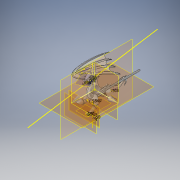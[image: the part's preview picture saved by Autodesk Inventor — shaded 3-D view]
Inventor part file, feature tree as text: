
AUTODESK INVENTOR PART (.ipt)
format: ipt  version: 2018 (Build 220112000, 112)  size: 5,354,496 bytes
history: native  units: in
note: dims shown in document units (in); Inventor stores cm internally (conversion verified against a paired STEP export)
features: sketch x122, plane x56, loft x36, fillet x16, other x14, projected_geometry x11, extrude x9, mirror x8, revolve x3, chamfer x2
ambient origin geometry x8: Origin, YZ Plane, XZ Plane, XY Plane, X Axis, Y Axis, Z Axis, Center Point
bodies: Solid1 (feature_tree)
feature tree (277):
  sketch  "Sketch4"  dims[d4=0.4in d5=0.4in]
  sketch  "Sketch5"  dims[d6=0.0in d7=0.0in]
  plane  "Work Plane2"
  loft  "Loft1"
  plane  "Work Plane4"
  sketch  "Sketch8"  dims[d10=0.0in d11=0.0in]
  plane  "Work Plane5"
  loft  "Loft2"
  extrude  "Extrusion1"  Depth=0.55in
  plane  "Work Plane6"
  extrude  "Extrusion2"  TaperAngle=0.0deg  [1 undecoded]
  extrude  "Extrusion3"  TaperAngle=0.0deg  [1 undecoded]
  chamfer  "Chamfer1"  Angle=90.0deg  [1 undecoded]
  sketch  "Sketch22"  dims[d39=0.45in d40=0.35in]
  plane  "Work Plane13"
  sketch  "Sketch23"  dims[d41=0.35in d42=0.5in]
  plane  "Work Plane14"
  loft  "Loft4"
  sketch  "Sketch25"  dims[d46=0.55in d47=0.0in]
  sketch  "Sketch26"  dims[d48=0.0in d49=0.35in d50=0.5in d51=0.0in d52=0.0in d53=90.0deg d54=0.0in d55=90.0deg d56=0.0in d57=90.0deg d58=1.0in]
  plane  "Work Plane15"
  sketch  "Sketch27"  dims[d59=1.0in d60=0.0in d61=0.25in]
  plane  "Work Plane16"
  loft  "Loft5"
  fillet  "Fillet1"  [1 undecoded]
  plane  "Work Plane17"
  sketch  "Sketch29"  dims[d64=1.2in d65=0.125in d66=0.15in d67=1.0in d68=0.0in d69=0.125in d70=0.0in]
  plane  "Work Plane18"
  loft  "Loft7"
  sketch  "Sketch32"  dims[d107=0.55in d108=-0.8in]
  plane  "Work Plane21"
  sketch  "Sketch35"  dims[d109=0.5in d110=0.5in]
  plane  "Work Plane22"
  loft  "Loft8"
  plane  "Work Plane23"
  sketch  "Sketch37"  dims[d112=0.89in d113=0.0in d114=90.0deg d115=0.0in d116=90.0deg]
  sketch  "Sketch38"  dims[d117=0.0in d118=90.0deg d119=0.65in d120=0.4in]
  sketch  "Sketch39"  dims[d121=0.5in d123=0.6in]
  plane  "Work Plane25"
  loft  "Loft9"
  sketch  "Sketch43"  dims[d132=0.15in d133=0.75in]
  sketch  "Sketch44"  dims[d134=0.3in d135=0.2in]
  sketch  "Sketch45"  dims[d136=0.5in d141=0.0in d142=90.0deg]
  plane  "Work Plane27"
  loft  "Loft11"
  fillet  "Fillet2"  [1 undecoded]
  other  "Work Point3"
  sketch  "Sketch48"  dims[d155=0.124in d156=90.0deg d157=-0.75in]
  sketch  "Sketch49"  dims[d158=1.0in d159=0.55in]
  plane  "Work Plane28"
  extrude  "Extrusion4"  TaperAngle=0.0deg  [1 undecoded]
  mirror  "Mirror3"
  extrude  "Extrusion6"  Depth=0.35in
  fillet  "Fillet3"  Radius=0.5in
  fillet  "Fillet4"  [1 undecoded]
  fillet  "Fillet12"  [1 undecoded]
  fillet  "Fillet9"  [1 undecoded]
  fillet  "Fillet10"  [1 undecoded]
  fillet  "Fillet11"  Radius=1.0in
  mirror  "Mirror4"
  mirror  "Mirror5"
  mirror  "Mirror6"
  plane  "Work Plane29"
  sketch  "Sketch52"  dims[d167=0.35in d168=0.7in]
  plane  "Work Plane30"
  sketch  "Sketch54"  dims[d169=0.65in d170=0.6in]
  sketch  "Sketch55"  dims[d171=0.2in d172=0.0in d173=90.0deg]
  plane  "Work Plane31"
  sketch  "Sketch56"  dims[d174=0.0in d175=90.0deg d176=0.0in d177=90.0deg d179=0.5in]
  sketch  "Sketch57"  dims[d180=-0.1in d181=0.2in]
  plane  "Work Plane34"
  sketch  "Sketch60"  dims[d182=0.28in d187=0.7in]
  loft  "Loft14"
  loft  "Loft15"
  sketch  "Sketch61"  dims[d188=0.7in d189=0.0in d190=90.0deg]
  sketch  "Sketch62"  dims[d191=0.0in d192=90.0deg d193=0.0in d194=90.0deg d196=0.125in]
  plane  "Work Plane35"
  loft  "Loft16"
  fillet  "Fillet14"  Radius=0.15in
  fillet  "Fillet15"  Radius=1.0in
  mirror  "Mirror7"
  fillet  "Fillet16"  Radius=0.125in
  sketch  "Sketch64"  dims[d200=1.25in d201=1.55in]
  sketch  "Sketch65"  dims[d202=0.175in d203=0.25in]
  plane  "Work Plane36"
  loft  "Loft17"
  loft  "Loft18"
  sketch  "Sketch70"  dims[d221=-0.45in]
  plane  "Work Plane37"
  sketch  "Sketch71"  dims[d222=0.4in]
  plane  "Work Plane38"
  revolve  "Revolution1"  [1 undecoded]
  extrude  "Extrusion7"  Depth=0.5in
  chamfer  "Chamfer2"  Angle=90.0deg  [1 undecoded]
  mirror  "Mirror8"
  fillet  "Fillet19"  [1 undecoded]
  plane  "Work Plane39"
  sketch  "Sketch74"  dims[d225=0.0in]
  sketch  "Sketch75"  dims[d226=0.45in]
  plane  "Work Plane40"
  revolve  "Revolution2"  [1 undecoded]
  fillet  "Fillet21"  Radius=0.4in
  sketch  "Sketch77"  dims[d228=0.0in]
  sketch  "Sketch78"  dims[d229=0.0in]
  plane  "Work Plane41"
  sketch  "Sketch79"  dims[d232=-0.4in]
  plane  "Work Plane42"
  loft  "Loft19"
  plane  "Work Plane43"
  extrude  "Extrusion8"  Depth=0.2in
  plane  "Work Plane44"
  sketch  "Sketch82"  dims[d235=0.0in]
  plane  "Work Plane45"
  sketch  "Sketch83"  dims[d236=0.0in]
  fillet  "Fillet22"  [1 undecoded]
  loft  "Loft21"
  sketch  "Sketch85"  dims[d238=0.525in]
  sketch  "Sketch86"  dims[d239=0.35in]
  sketch  "Sketch87"  dims[d240=0.45in]
  sketch  "Sketch88"  dims[d241=0.4in]
  plane  "Work Plane46"
  sketch  "Sketch89"  dims[d256=0.3in]
  plane  "Work Plane47"
  sketch  "Sketch90"  dims[d257=0.0in d258=90.0deg]
  plane  "Work Plane48"
  sketch  "Sketch91"  dims[d259=0.0in d260=90.0deg]
  other  "Work Point4"
  loft  "Loft22"
  plane  "Work Plane49"
  sketch  "Sketch92"  dims[d261=0.0in d262=90.0deg]
  other  "Work Point5"
  loft  "Loft23"
  plane  "Work Plane50"
  sketch  "Sketch93"  dims[d263=0.0in d264=90.0deg]
  other  "Work Point6"
  loft  "Loft24"
  plane  "Work Plane51"
  sketch  "Sketch94"  dims[d265=0.0in d266=90.0deg]
  sketch  "Sketch95"  dims[d267=0.0in d268=90.0deg]
  other  "Work Point7"
  loft  "Loft25"
  plane  "Work Plane52"
  sketch  "Sketch96"  dims[d270=0.45in d271=0.55in d272=0.89in]
  sketch  "Sketch97"  dims[d276=0.4in]
  other  "Work Point8"
  loft  "Loft26"
  mirror  "Mirror9"
  sketch  "Sketch98"  dims[d277=0.065in]
  sketch  "Sketch99"  dims[d278=0.5in]
  sketch  "Sketch100"  dims[d279=0.55in]
  plane  "Work Plane53"
  sketch  "Sketch101"  dims[d280=0.5622in]
  sketch  "Sketch102"  dims[d281=0.5544in]
  other  "Work Point9"
  loft  "Loft27"
  plane  "Work Plane54"
  loft  "Loft28"
  sketch  "Sketch105"  dims[d287=0.0in d288=90.0deg]
  plane  "Work Plane55"
  loft  "Loft29"
  sketch  "Sketch107"  dims[d291=0.05in]
  plane  "Work Plane56"
  loft  "Loft30"
  sketch  "Sketch109"  dims[d293=0.1388in]
  plane  "Work Plane57"
  loft  "Loft31"
  sketch  "Sketch111"  dims[d295=0.4in]
  plane  "Work Plane58"
  loft  "Loft32"
  sketch  "Sketch113"  dims[d297=0.6in]
  sketch  "Sketch114"  dims[d298=0.2in]
  plane  "Work Plane59"
  revolve  "Revolution3"  Angle=90.0deg
  extrude  "Extrusion9"  TaperAngle=0.0deg  [1 undecoded]
  mirror  "Mirror10"
  fillet  "Fillet23"  Radius=0.5in
  plane  "Work Plane60"
  sketch  "Sketch119"  dims[d303=0.0in d304=90.0deg]
  plane  "Work Plane61"
  sketch  "Sketch120"  dims[d305=0.5in]
  plane  "Work Plane62"
  loft  "Loft33"
  loft  "Loft34"
  plane  "Work Plane65"
  sketch  "Sketch122"  dims[d307=0.75in]
  plane  "Work Plane66"
  sketch  "Sketch123"  dims[d308=0.2in]
  plane  "Work Plane68"
  sketch  "Sketch124"  dims[d309=0.3in]
  other  "Work Point10"
  loft  "Loft35"
  sketch  "Sketch126"  dims[d312=0.0in d313=90.0deg]
  sketch  "Sketch127"  dims[d314=0.1in]
  other  "Work Point11"
  loft  "Loft36"
  fillet  "Fillet24"  Radius=0.125in
  sketch  "Sketch128"  dims[d315=0.4in]
  sketch  "Sketch129"  dims[d316=0.75in]
  other  "Work Point12"
  loft  "Loft37"
  extrude  "Extrusion10"  Depth=1.55in
  plane  "Work Plane69"
  loft  "Loft38"
  sketch  "Sketch132"  dims[d319=1.3in]
  plane  "Work Plane71"
  sketch  "Sketch133"  dims[d320=0.45in]
  sketch  "Sketch134"  dims[d321=0.6in]
  loft  "Loft39"
  loft  "Loft40"
  loft  "Loft41"
  loft  "Loft42"
  sketch  "Sketch6"  dims[d8=0.55in d9=0.55in]
  sketch  "Sketch9"  dims[d12=0.5in d13=0.0in d14=90.0deg d15=0.0in d16=90.0deg]
  other  "Edges1"
  sketch  "Sketch10"  dims[d17=0.0in d18=90.0deg d19=3.0in]
  projected_geometry  "Projected Loop2"
  projected_geometry  "Projected Loop3"
  sketch  "Sketch11"  dims[d21=0.65in d34=0.0in d35=0.0in]
  projected_geometry  "Projected Loop4"
  sketch  "Sketch12"  dims[d36=0.0in d38=0.0in]
  projected_geometry  "Projected Loop5"
  sketch  "Sketch24"  dims[d43=-0.7in d44=0.35in d45=0.0in]
  sketch  "Sketch28"  dims[d62=2.0in d63=0.6in]
  sketch  "Sketch30"  dims[d75=0.03in d76=0.125in d77=45.0deg d103=0.1in]
  sketch  "Sketch31"  dims[d104=0.5in d106=0.45in]
  plane  "Work Plane20"
  sketch  "Sketch36"  dims[d111=0.55in]
  projected_geometry  "Projected Loop8"
  sketch  "Sketch40"  dims[d124=0.0in d125=0.2in d126=0.0in d127=90.0deg]
  sketch  "Sketch41"  dims[d128=0.0in d129=90.0deg d130=0.0in d131=90.0deg]
  plane  "Work Plane26"
  sketch  "Sketch46"  dims[d143=0.0in d144=90.0deg d146=0.5in d147=0.45in d148=0.55in d149=0.89in]
  sketch  "Sketch47"  dims[d150=45.0deg d154=0.535in]
  sketch  "Sketch50"  dims[d160=0.0in d161=90.0deg d162=0.0in d163=90.0deg]
  sketch  "Sketch51"  dims[d164=0.0in d165=90.0deg d166=-0.5in]
  projected_geometry  "Projected Loop9"
  other  "Edges4"
  other  "Edges5"
  sketch  "Sketch63"  dims[d198=0.5in d199=1.2in]
  projected_geometry  "Projected Loop10"
  sketch  "Sketch66"  dims[d204=0.25in d205=0.0in d208=0.125in d209=0.0in]
  sketch  "Sketch67"  dims[d210=0.075in d211=0.05in]
  sketch  "Sketch68"  dims[d216=0.075in d217=0.05in]
  sketch  "Sketch69"  dims[d218=0.065in d219=0.065in]
  projected_geometry  "Projected Loop11"
  sketch  "Sketch72"  dims[d223=0.4in]
  sketch  "Sketch73"  dims[d224=0.0in]
  projected_geometry  "Projected Loop12"
  sketch  "Sketch76"  dims[d227=0.6in]
  sketch  "Sketch80"  dims[d233=0.0in]
  sketch  "Sketch81"  dims[d234=0.0in]
  projected_geometry  "Projected Loop13"
  sketch  "Sketch84"  dims[d237=0.35in]
  projected_geometry  "Projected Loop14"
  sketch  "Sketch103"  dims[d284=0.52in]
  sketch  "Sketch104"  dims[d285=0.0in d286=90.0deg]
  sketch  "Sketch106"  dims[d289=0.0in d290=90.0deg]
  sketch  "Sketch108"  dims[d292=0.125in]
  sketch  "Sketch110"  dims[d294=0.65in]
  sketch  "Sketch112"  dims[d296=0.5in]
  sketch  "Sketch115"  dims[d299=0.0in d300=90.0deg]
  sketch  "Sketch116"  dims[d301=0.0in d302=90.0deg]
  sketch  "Sketch121"  dims[d306=0.8176in]
  other  "Edges6"
  sketch  "Sketch125"  dims[d310=0.0in d311=90.0deg]
  sketch  "Sketch130"  dims[d317=90.0deg]
  sketch  "Sketch131"  dims[d318=0.75in]
  plane  "Work Plane70"
  sketch  "Sketch136"  dims[d322=0.2in d323=0.0in]
  sketch  "Sketch137"  dims[d324=0.1in d325=0.125in d326=45.0deg]
  sketch  "Sketch138"  dims[d327=0.5944in]
  sketch  "Sketch139"  dims[d330=10.0in]
  sketch  "Sketch140"  dims[d331=10.0in]
  sketch  "Sketch141"  dims[d332=2.0in]
  sketch  "Sketch142"  dims[d333=0.6252in]
  sketch  "Sketch143"  dims[d334=0.475in]
  sketch  "Sketch144"  dims[d335=0.045in d336=-1.0in d337=2.5in d338=0.3in d339=0.6in d340=1.25in d341=1.25in d344=30.0deg d346=0.125in d347=1.0in d348=0.5in d349=0.5in d350=0.5in d351=0.225in d352=0.25in d353=-0.4in d354=0.2in d355=0.06in d356=0.0in d357=90.0deg d358=0.0in d359=90.0deg d360=0.5in d361=0.5in d362=0.3125in d363=0.0in d364=0.15in d365=0.02in d366=0.175in d367=-0.6in d368=0.12in d376=0.03in d377=0.25in d378=0.0in d379=90.0deg d380=0.3937in d381=90.0deg d382=0.0in d383=90.0deg d384=0.2in d385=0.45in d388=0.2in d389=0.18in d391=0.175in d392=0.555in d393=0.27in d394=0.28in d395=0.645in d396=0.655in d397=0.678in d398=0.2in d399=0.2in d401=0.3in d402=0.35in d403=0.6in d404=0.55in d405=0.325in d406=0.6in d407=0.25in d408=0.5in d409=0.2in d410=0.45in d411=0.2in d412=0.18in d413=0.175in d414=0.555in d415=0.27in d416=0.28in d417=0.645in d418=0.655in d419=0.678in d424=-0.5in d425=0.2in d426=0.45in d427=0.2in d428=0.18in d429=0.175in d430=0.555in d431=0.27in d432=0.28in d433=0.645in d434=0.655in d435=0.678in d440=0.0in d441=90.0deg d442=0.0in d443=90.0deg d444=0.0in d445=90.0deg d446=0.15in d447=0.14in d448=0.0in d449=90.0deg d450=0.0in d451=90.0deg d452=0.0in d453=90.0deg d454=0.125in d455=0.0in d456=90.0deg d457=0.0in d458=90.0deg d459=0.0in d460=90.0deg d461=0.12in d462=0.08in d463=0.2in d464=0.45in d465=0.2in d466=0.18in d467=0.175in d468=0.555in d469=0.27in d470=0.28in d471=0.645in d472=0.655in d473=0.678in d474=0.2in d476=0.3in d477=0.12in d478=0.08in d479=0.1in d480=0.6in d481=0.135in d482=0.0in d483=90.0deg d484=0.0in d485=90.0deg d486=0.0in d487=90.0deg d488=0.45in d489=0.05in d490=0.08in d491=0.1in d492=0.5in d493=0.16in d494=0.0in d495=90.0deg d496=0.0in d497=90.0deg d498=0.0in d499=90.0deg d501=0.2in d503=0.025in d505=0.2in d506=0.325in d507=0.496in d508=0.1in d510=0.2in d511=0.2in d512=0.2in d513=0.2in d514=0.275in d515=0.105in d516=0.1752in d517=0.29in d518=0.25in d519=0.275in d520=0.08in d521=0.065in d522=0.33in d523=0.3in d524=0.07in d525=0.16in d526=0.415in d527=0.04in d529=0.16in d530=0.6in d531=0.2in d532=0.0in d533=90.0deg d534=0.0in d535=90.0deg d536=0.0in d537=90.0deg d538=0.155in d539=0.65in d540=0.31in d541=0.0in d542=90.0deg d543=0.0in d544=90.0deg d545=0.0in d546=90.0deg d547=0.7in d548=0.24in d549=0.14in d550=0.0in d551=90.0deg d552=0.0in d553=90.0deg d554=0.0in d555=90.0deg d556=0.6in d557=0.22in d558=0.13in d559=0.0in d560=90.0deg d561=0.0in d562=90.0deg d563=0.0in d564=90.0deg d565=0.6in d566=0.04in d567=0.12in d568=0.0in d569=90.0deg d570=0.0in d571=90.0deg d572=0.0in d573=90.0deg d574=0.6in d575=0.24in d576=0.11in d577=0.0in d578=90.0deg d579=0.0in d580=90.0deg d581=0.0in d582=90.0deg d583=0.01in d585=0.35in d594=60.0deg d603=0.4in d604=0.2in d605=0.085in d607=0.08in d608=0.055in d611=1.0in d612=0.0in d613=0.031in d618=0.1059in d620=0.1091in d621=0.05in d623=0.75in d625=0.07in d627=0.2in d631=1.2in d632=0.01in d633=2.75in d634=0.15in d635=0.5in d636=0.255in d637=0.4in d638=0.55in d640=0.0in d642=-0.15in d643=0.07in d644=0.7in d645=0.25in d646=0.0in d647=90.0deg d650=0.0in d651=90.0deg d652=0.0in d653=90.0deg d654=0.05in d655=1.0in d656=0.05in d662=0.05in d668=-2.0in d669=0.5in d670=0.2in d671=0.08in d672=0.0in d673=90.0deg d674=0.0in d675=90.0deg d676=0.0in d677=90.0deg d678=0.06in d679=0.055in d680=0.175in d681=0.0in d682=90.0deg d683=0.0in d684=90.0deg d685=0.0in d686=90.0deg d687=0.01in d688=0.06in d689=0.05in d690=0.08in d691=0.175in d692=0.0in d693=90.0deg d694=0.0in d695=90.0deg d696=0.0in d697=90.0deg d698=0.05in d699=1.0in d700=0.0in d701=0.3in d702=0.13in d703=0.15in d704=0.15in d705=0.16in d706=0.12in d707=0.12in d708=0.14in d709=0.1in d710=0.1in d711=0.1in d712=0.1in d713=0.0in d714=90.0deg d715=0.0in d716=90.0deg d717=0.3937in d718=90.0deg d719=0.15in d720=0.15in d721=0.125in d722=0.015in d723=0.015in d724=0.0in d725=90.0deg d726=0.0in d727=90.0deg d730=0.0in d731=90.0deg d732=0.07in d733=0.07in d734=0.07in d735=0.07in d736=0.209in d737=0.05in d738=0.0in d739=0.1in d740=0.24in d741=0.076in d742=0.0in d743=0.24in d744=0.0in d745=90.0deg d746=0.0in d747=90.0deg d748=0.0in d749=90.0deg d750=0.09in d751=0.07in d752=0.365in d753=0.355in d754=0.0in d755=90.0deg d756=0.0in d757=90.0deg d758=0.0in d759=90.0deg d760=0.085in d761=0.0in d762=90.0deg d763=0.0in d764=90.0deg d765=0.0in d766=90.0deg]
note: 16 required parameter values undecoded (feature->parameter linkage not recoverable at this tier; creation-order binding heuristic only, values carry confidence <= 0.55)